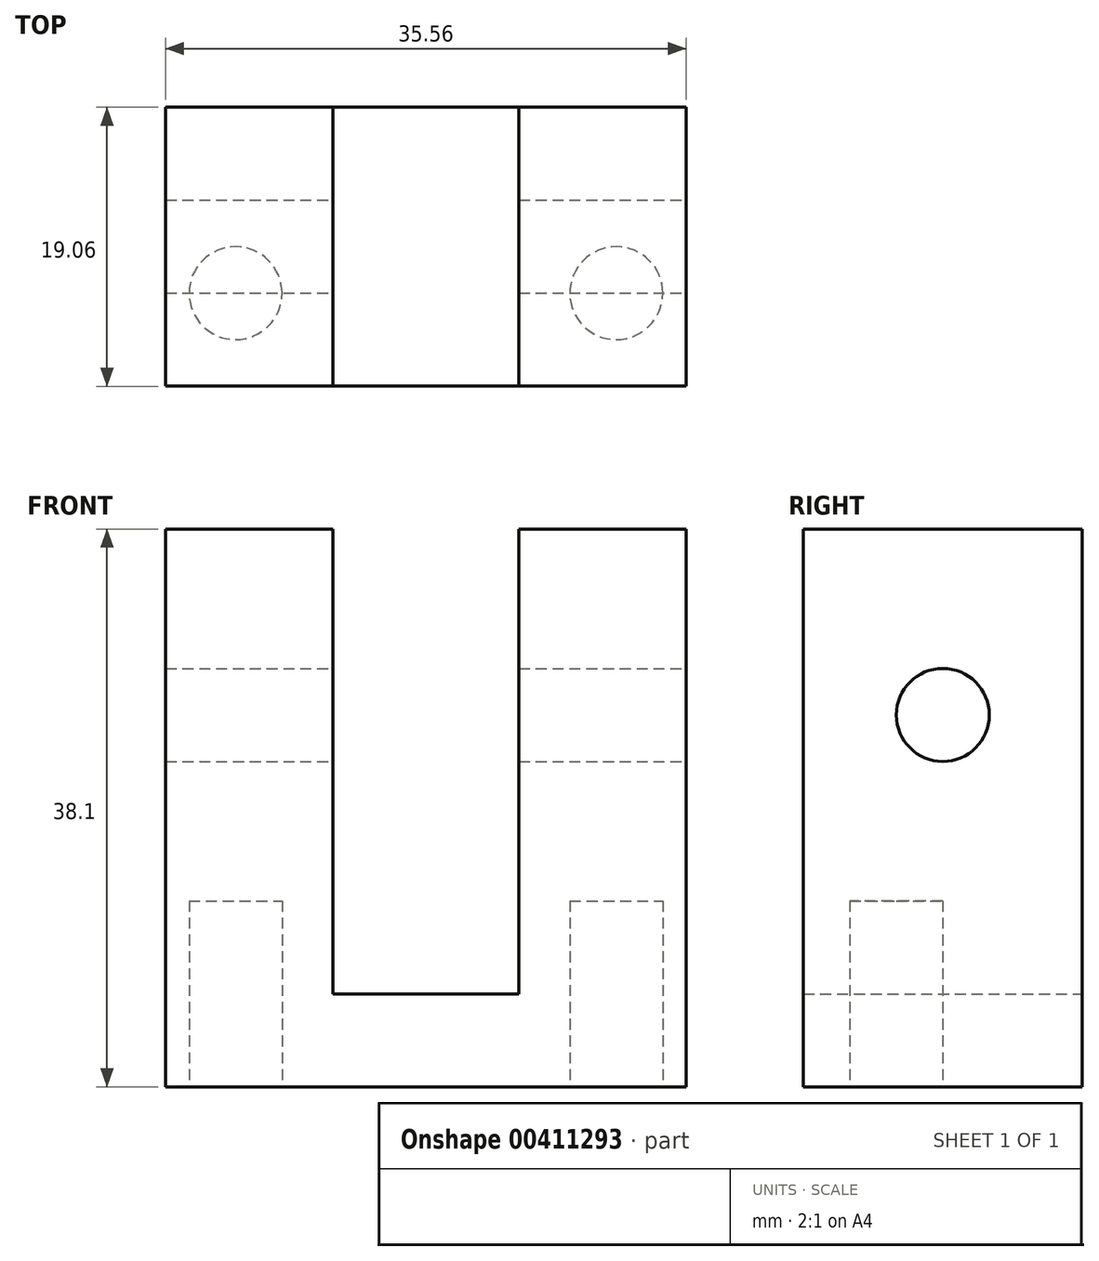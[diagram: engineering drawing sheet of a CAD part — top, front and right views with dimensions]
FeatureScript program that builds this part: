
annotation { "Feature Type Name" : "Feature", "Feature Type Description" : "" }
export const myFeature = defineFeature(function(context is Context, id is Id, definition is map)
    precondition{}
    {
        {
            var Q0;
            Q0=qCreatedBy(makeId("Front.planeOp"),FACE);
            var sketch = newSketch(context, id + "F0", { "sketchPlane" : qUnion([Q0])});
            skLineSegment(sketch, "E0", {"start": v(-17.78, 12.7) * mm, "end": v(-17.78, -25.4) * mm});
            skLineSegment(sketch, "E1", {"start": v(-17.78, -25.4) * mm, "end": v(17.78, -25.4) * mm});
            skLineSegment(sketch, "E2", {"start": v(17.78, -25.4) * mm, "end": v(17.78, 12.7) * mm});
            skLineSegment(sketch, "E3", {"start": v(17.78, 12.7) * mm, "end": v(6.35, 12.7) * mm});
            skLineSegment(sketch, "E4", {"start": v(6.35, 12.7) * mm, "end": v(6.35, -19.05) * mm});
            skLineSegment(sketch, "E5", {"start": v(6.35, -19.05) * mm, "end": v(-6.35, -19.05) * mm});
            skLineSegment(sketch, "E6", {"start": v(-6.35, -19.05) * mm, "end": v(-6.35, 12.7) * mm});
            skLineSegment(sketch, "E7", {"start": v(-6.35, 12.7) * mm, "end": v(-17.78, 12.7) * mm});
            skSolve(sketch);
        }
        {
            var Q0;
            Q0 = qSketchRegion(id + "F0", true);
            extrude(context, id + "F1", {"entities" : qUnion([Q0]), "endBound" : BoundingType.SYMMETRIC, "depth" : 19.05 * mm});
        }
        {
            var Q0;
            Q0=makeQuery(id+"F1.opExtrude","SWEPT_FACE",FACE,{"disambiguationData":[OSD([sQuery(id+"F0.wireOp",EDGE,"E2")])]});
            var sketch = newSketch(context, id + "F2", { "sketchPlane" : qUnion([Q0])});
            skCircle(sketch, "E8", {"center": v(0, 0) * mm, "radius": 3.17 * mm});
            skSolve(sketch);
        }
        {
            var Q0;
            Q0 = qSketchRegion(id + "F2", true);
            var Q1;
            Q1=makeQuery(id+"F1.opExtrude","SWEPT_FACE",FACE,{"disambiguationData":[OSD([sQuery(id+"F0.wireOp",EDGE,"E0")])]});
            extrude(context, id + "F3", {"entities" : qUnion([Q0]), "operationType" : NewBodyOperationType.REMOVE, "endBound" : BoundingType.UP_TO_SURFACE, "oppositeDirection" : true, "endBoundEntityFace" : qUnion([Q1]), "depth" : 25.4 * mm});
        }
        {
            var Q0;
            Q0=makeQuery(id+"F1.opExtrude","SWEPT_FACE",FACE,{"disambiguationData":[OSD([sQuery(id+"F0.wireOp",EDGE,"E1")])]});
            var sketch = newSketch(context, id + "F4", { "sketchPlane" : qUnion([Q0])});
            skCircle(sketch, "E9", {"center": v(-13, 3.17) * mm, "radius": 3.18 * mm});
            skCircle(sketch, "E10", {"center": v(13, 3.18) * mm, "radius": 3.18 * mm});
            skSolve(sketch);
        }
        {
            var Q0;
            Q0 = qSketchRegion(id + "F4", true);
            extrude(context, id + "F5", {"entities" : qUnion([Q0]), "operationType" : NewBodyOperationType.REMOVE, "oppositeDirection" : true, "depth" : 12.7 * mm});
        }
    });
